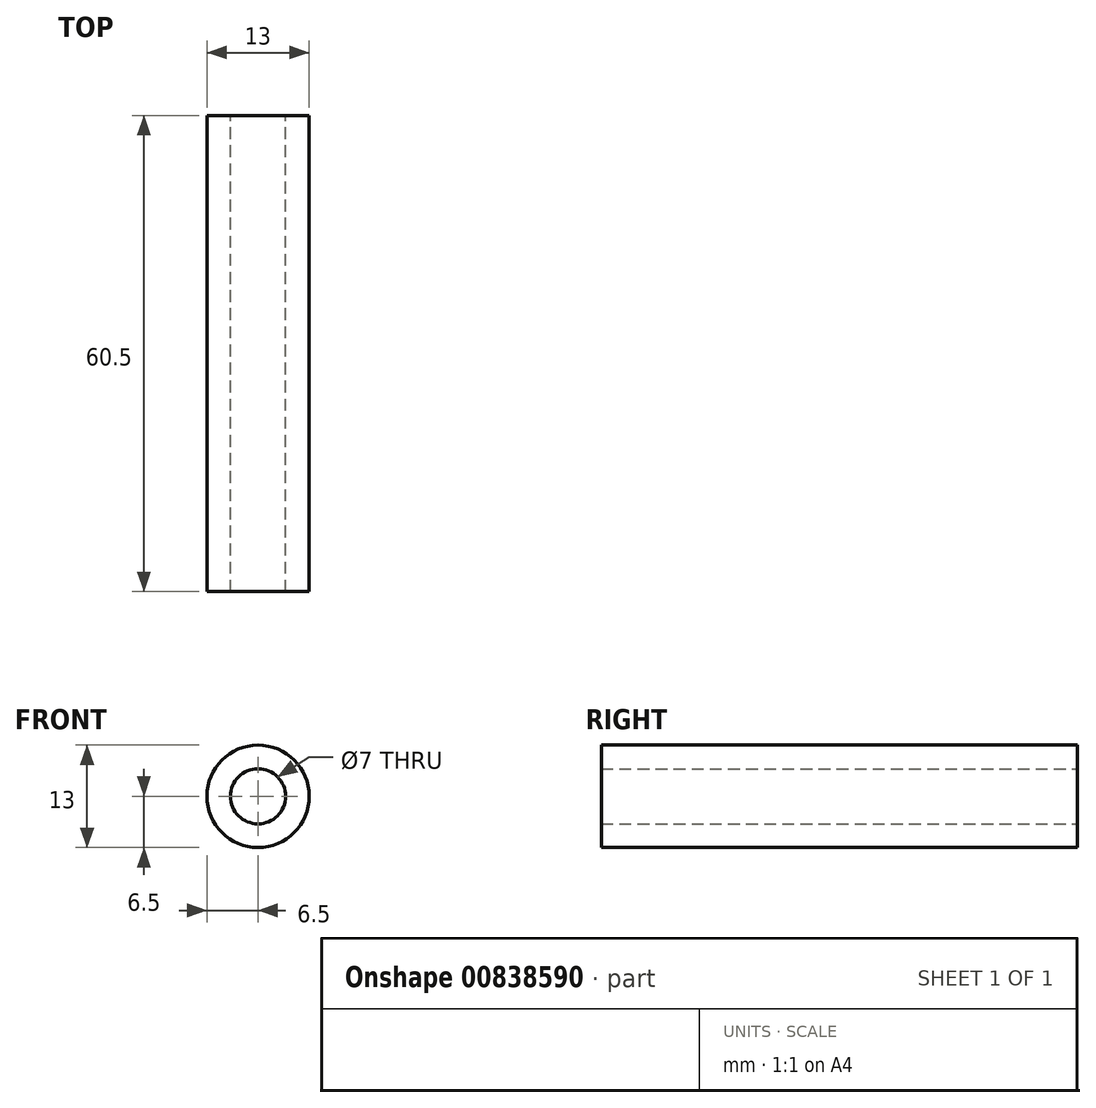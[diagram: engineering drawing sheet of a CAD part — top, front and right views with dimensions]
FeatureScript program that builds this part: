
annotation { "Feature Type Name" : "Feature", "Feature Type Description" : "" }
export const myFeature = defineFeature(function(context is Context, id is Id, definition is map)
    precondition{}
    {
        {
            var Q0;
            Q0=qCreatedBy(makeId("Front.planeOp"),FACE);
            var sketch = newSketch(context, id + "F0", { "sketchPlane" : qUnion([Q0])});
            skCircle(sketch, "E0", {"center": v(0, 0) * mm, "radius": 6.5 * mm});
            skCircle(sketch, "E1.0", {"center": v(0, 0) * mm, "radius": 3.5 * mm});
            skSolve(sketch);
        }
        {
            var Q0;
            Q0=makeQuery(id+"F0.imprint","IMPRINT",FACE,{"disambiguationData":[TD([[makeQuery(id+"F0.imprint","IMPRINT",EDGE,{"derivedFrom":sQuery(id+"F0.wireOp",EDGE,"E0")}),1.0]])]});
            extrude(context, id + "F1", {"entities" : qUnion([Q0]), "depth" : 60.5 * mm, "offsetDistance" : 25 * mm});
        }
    });
